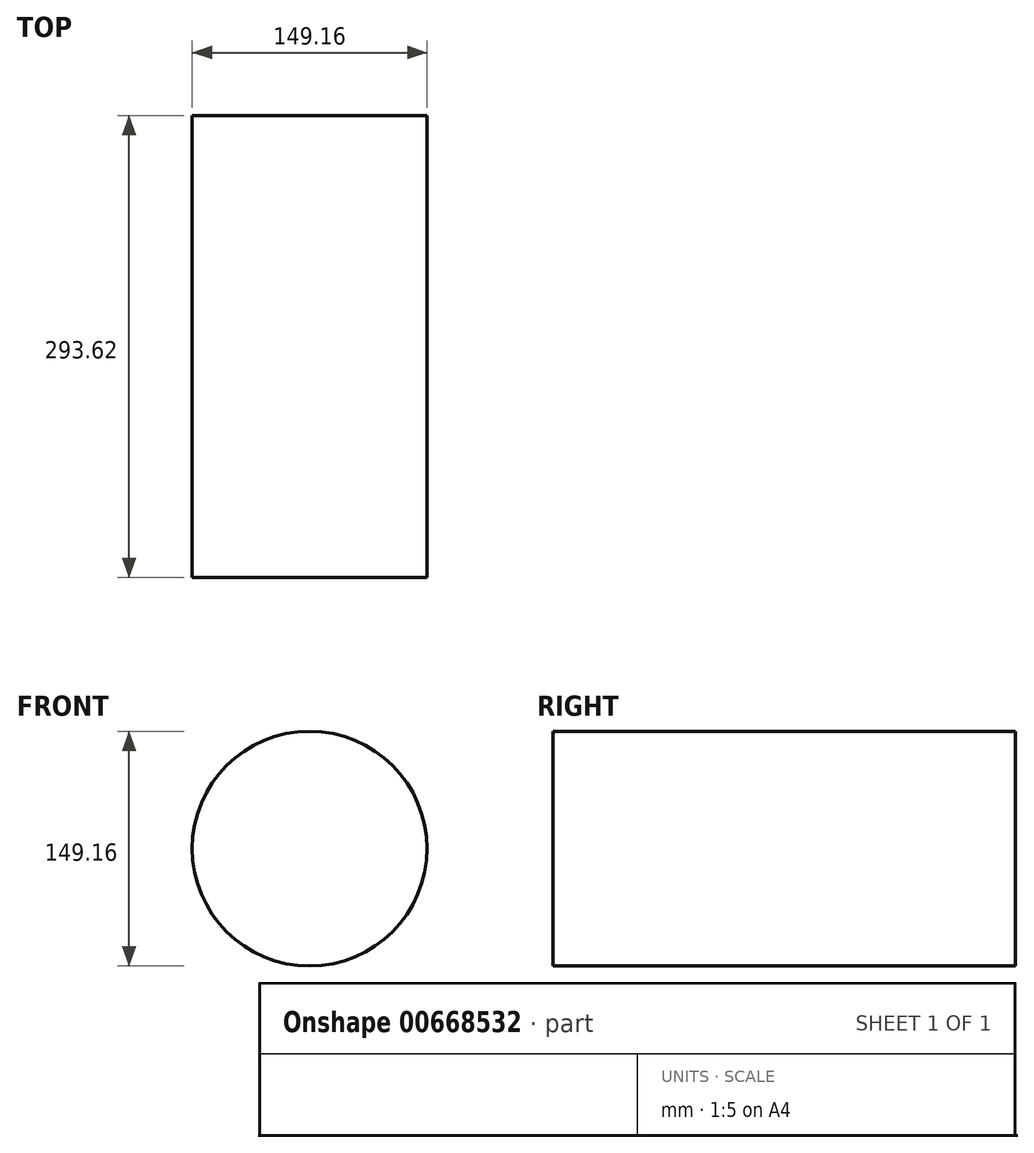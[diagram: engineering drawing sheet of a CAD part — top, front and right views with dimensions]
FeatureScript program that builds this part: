
annotation { "Feature Type Name" : "Feature", "Feature Type Description" : "" }
export const myFeature = defineFeature(function(context is Context, id is Id, definition is map)
    precondition{}
    {
        {
            var Q0;
            Q0=qCreatedBy(makeId("Front.planeOp"),FACE);
            var sketch = newSketch(context, id + "F0", { "sketchPlane" : qUnion([Q0])});
            skCircle(sketch, "E0", {"center": v(0, 0) * mm, "radius": 74.58 * mm});
            skSolve(sketch);
        }
        {
            var Q0;
            Q0 = qSketchRegion(id + "F0", true);
            extrude(context, id + "F1", {"entities" : qUnion([Q0]), "oppositeDirection" : true, "depth" : 293.62 * mm, "offsetDistance" : 25.4 * mm});
        }
    });
